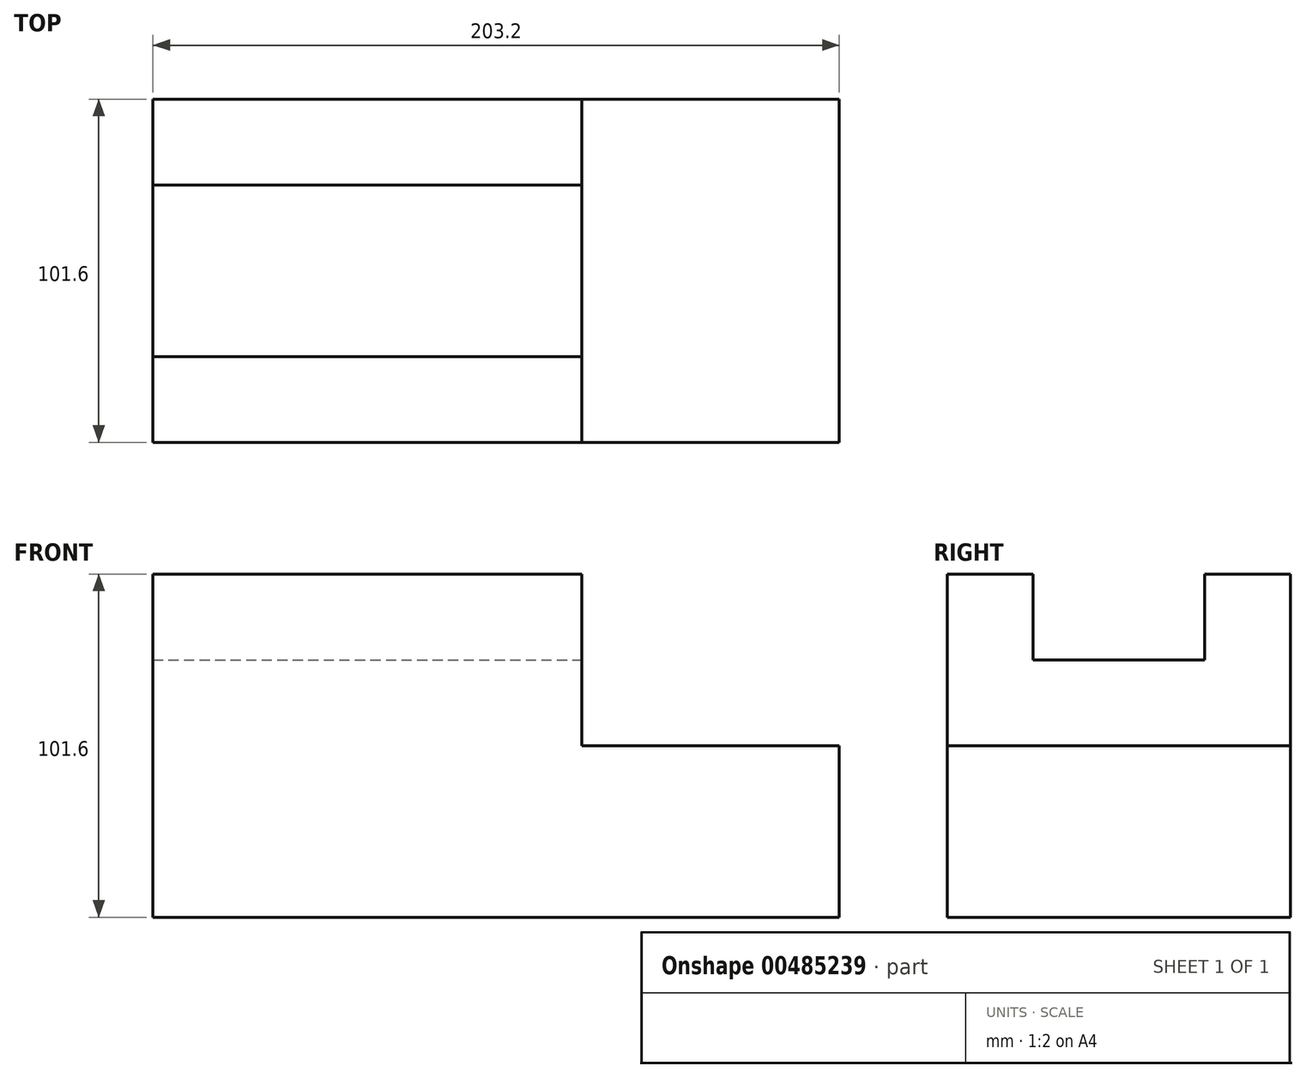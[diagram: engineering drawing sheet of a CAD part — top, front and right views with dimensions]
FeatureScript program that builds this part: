
annotation { "Feature Type Name" : "Feature", "Feature Type Description" : "" }
export const myFeature = defineFeature(function(context is Context, id is Id, definition is map)
    precondition{}
    {
        {
            var Q0;
            Q0=qCreatedBy(makeId("Front.planeOp"),FACE);
            var sketch = newSketch(context, id + "F0", { "sketchPlane" : qUnion([Q0])});
            skLineSegment(sketch, "E0.bottom", {"start": v(-78.28, 50.8) * mm, "end": v(48.72, 50.8) * mm});
            skLineSegment(sketch, "E0.top", {"start": v(-78.28, -50.8) * mm, "end": v(48.72, -50.8) * mm});
            skLineSegment(sketch, "E0.left", {"start": v(-78.28, 50.8) * mm, "end": v(-78.28, -50.8) * mm});
            skLineSegment(sketch, "E0.right", {"start": v(48.72, 50.8) * mm, "end": v(48.72, -50.8) * mm});
            skLineSegment(sketch, "E1.bottom", {"start": v(48.72, -50.8) * mm, "end": v(124.92, -50.8) * mm});
            skLineSegment(sketch, "E1.top", {"start": v(48.72, 0) * mm, "end": v(124.92, 0) * mm});
            skLineSegment(sketch, "E1.left", {"start": v(48.72, -50.8) * mm, "end": v(48.72, 0) * mm});
            skLineSegment(sketch, "E1.right", {"start": v(124.92, -50.8) * mm, "end": v(124.92, 0) * mm});
            skSolve(sketch);
        }
        {
            var Q0;
            Q0 = qSketchRegion(id + "F0", true);
            extrude(context, id + "F1", {"entities" : qUnion([Q0]), "depth" : 101.6 * mm});
        }
        {
            var Q0;
            Q0=makeQuery(id+"F1.opExtrude","SWEPT_FACE",FACE,{"disambiguationData":[OSD([sQuery(id+"F0.wireOp",EDGE,"E0.bottom")])]});
            var sketch = newSketch(context, id + "F2", { "sketchPlane" : qUnion([Q0])});
            skLineSegment(sketch, "E2.bottom", {"start": v(-78.28, -25.4) * mm, "end": v(48.72, -25.4) * mm});
            skLineSegment(sketch, "E2.top", {"start": v(-78.28, -76.2) * mm, "end": v(48.72, -76.2) * mm});
            skLineSegment(sketch, "E2.left", {"start": v(-78.28, -25.4) * mm, "end": v(-78.28, -76.2) * mm});
            skLineSegment(sketch, "E2.right", {"start": v(48.72, -25.4) * mm, "end": v(48.72, -76.2) * mm});
            skSolve(sketch);
        }
        {
            var Q0;
            Q0=makeQuery(id+"F2.imprint","IMPRINT",FACE,{"disambiguationData":[TD([[makeQuery(id+"F2.imprint","IMPRINT",EDGE,{"derivedFrom":sQuery(id+"F2.wireOp",EDGE,"E2.bottom")}),-1.0]])]});
            extrude(context, id + "F3", {"entities" : qUnion([Q0]), "operationType" : NewBodyOperationType.REMOVE, "oppositeDirection" : true, "depth" : 25.4 * mm});
        }
    });
